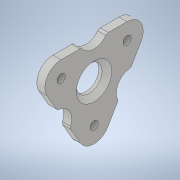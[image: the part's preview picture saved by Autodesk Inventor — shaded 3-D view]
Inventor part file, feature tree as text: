
AUTODESK INVENTOR PART (.ipt)
format: ipt  version: 2021 (Build 250183000, 183)  size: 189,440 bytes
history: native  units: in
note: dims shown in document units (in); Inventor stores cm internally (conversion verified against a paired STEP export)
features: extrude x2, sketch x2, fillet x1, chamfer x1
ambient origin geometry x8: Origin, YZ Plane, XZ Plane, XY Plane, X Axis, Y Axis, Z Axis, Center Point
bodies: Solid1 (feature_tree)
feature tree (6):
  extrude  "Extrusion1"  Depth=0.125in TaperAngle=360.0deg
  fillet  "Fillet2"  Radius=0.125in
  extrude  "Extrusion3"  Depth=0.125in
  chamfer  "Chamfer5"  Distance=0.3153in
  sketch  "Sketch1"  dims[d4=0.3125in d5=0.0in d26=1.1811in d28=360.0deg d30=0.125in]
  sketch  "Sketch5"  dims[d34=1.25in d35=1.135in d36=0.3153in d37=1.25in d38=1.25in d39=60.0deg d40=60.0deg d41=0.2903in d42=2.1897in d43=2.1897in d44=0.0in d45=1.6222in d46=0.0in d47=2.4668in d48=3.1515in d49=0.0in d50=3.1515in d51=0.625in d52=0.625in d53=0.9375in d54=3.1515in d55=1.363in d56=1.363in d57=1.6222in d58=0.0in d59=1.6222in d60=2.4668in d61=2.4668in d62=0.0in d63=2.4668in d64=1.6222in d65=2.839in d66=3.1515in d67=0.0in d68=3.1515in d69=0.9375in d70=1.0in d71=1.0in d72=0.0in d76=0.1875in d77=0.125in d78=45.0deg]
